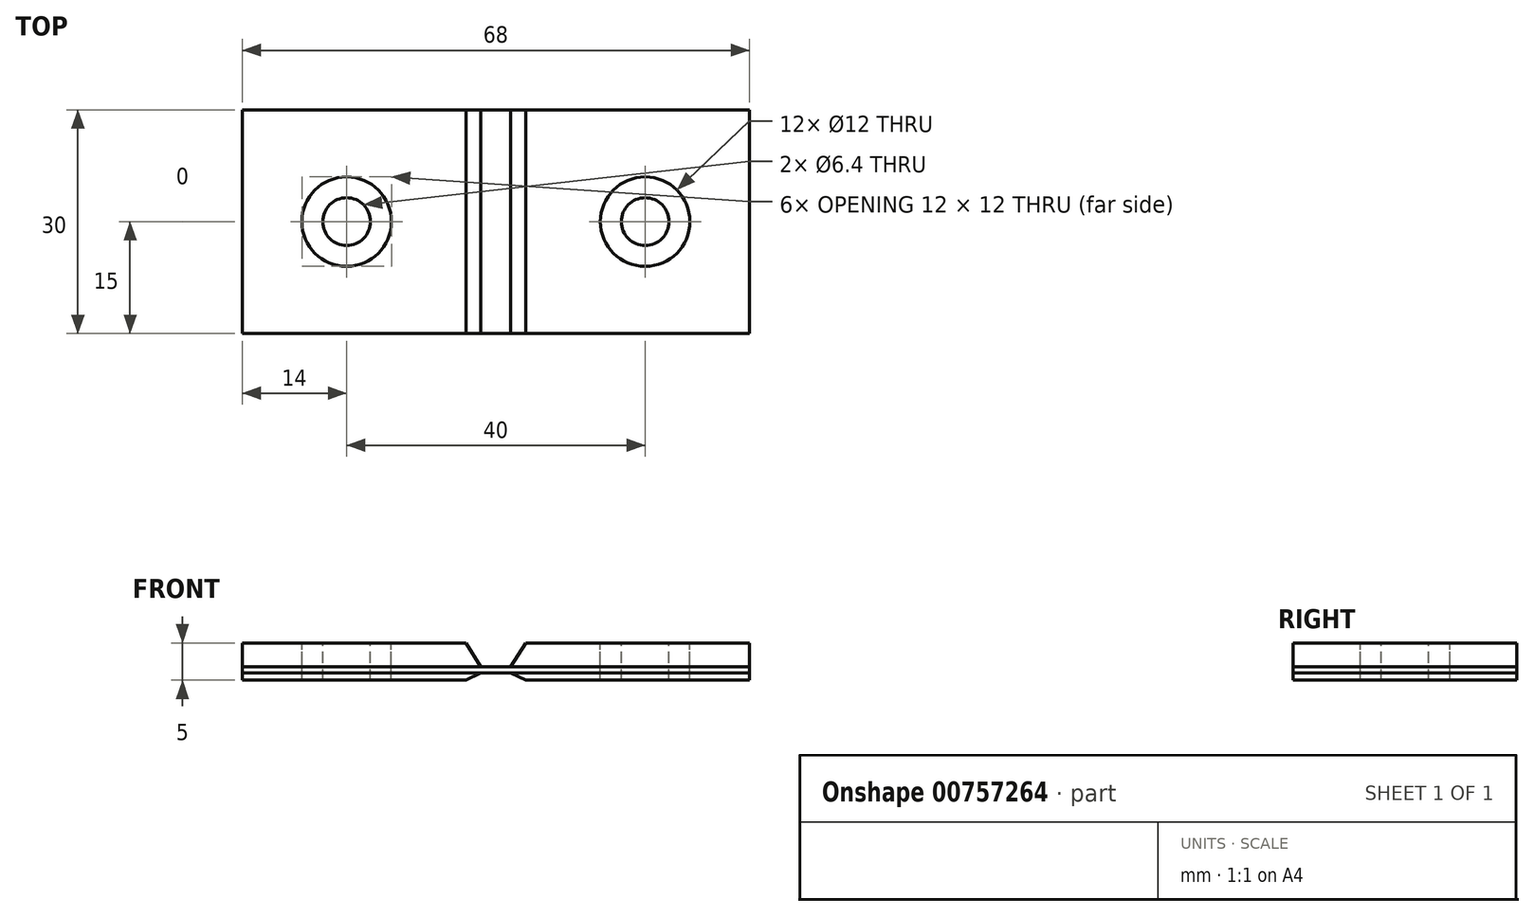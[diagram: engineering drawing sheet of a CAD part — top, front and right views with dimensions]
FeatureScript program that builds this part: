
annotation { "Feature Type Name" : "Feature", "Feature Type Description" : "" }
export const myFeature = defineFeature(function(context is Context, id is Id, definition is map)
    precondition{}
    {
        {
            var Q0;
            Q0=qCreatedBy(makeId("Front.planeOp"),FACE);
            var sketch = newSketch(context, id + "F0", { "sketchPlane" : qUnion([Q0])});
            skLineSegment(sketch, "E0", {"start": v(-34, 0) * mm, "end": v(-34, 5) * mm});
            skLineSegment(sketch, "E1", {"start": v(-34, 5) * mm, "end": v(-4, 5) * mm});
            skLineSegment(sketch, "E2", {"start": v(-4, 5) * mm, "end": v(-2, 1.8) * mm});
            skLineSegment(sketch, "E3", {"start": v(-2, 1.8) * mm, "end": v(2, 1.8) * mm});
            skLineSegment(sketch, "E4", {"start": v(2, 1.8) * mm, "end": v(4, 5) * mm});
            skLineSegment(sketch, "E5", {"start": v(4, 5) * mm, "end": v(34, 5) * mm});
            skLineSegment(sketch, "E6", {"start": v(34, 5) * mm, "end": v(34, 0) * mm});
            skLineSegment(sketch, "E7", {"start": v(34, 0) * mm, "end": v(4, 0) * mm});
            skLineSegment(sketch, "E8", {"start": v(4, 0) * mm, "end": v(2, 1) * mm});
            skLineSegment(sketch, "E9", {"start": v(2, 1) * mm, "end": v(-2, 1) * mm});
            skLineSegment(sketch, "E10", {"start": v(-2, 1) * mm, "end": v(-4, 0) * mm});
            skLineSegment(sketch, "E11", {"start": v(-4, 0) * mm, "end": v(-34, 0) * mm});
            skSolve(sketch);
        }
        {
            var Q0;
            Q0 = qSketchRegion(id + "F0", true);
            extrude(context, id + "F1", {"entities" : qUnion([Q0]), "depth" : 30 * mm, "offsetDistance" : 25 * mm});
        }
        {
            var Q0;
            Q0=makeQuery(id+"F1.opExtrude","CAP_FACE",FACE,{"disambiguationData":[OSD([sQuery(id+"F0.wireOp",EDGE,"E0"),sQuery(id+"F0.wireOp",EDGE,"E1"),sQuery(id+"F0.wireOp",EDGE,"E2"),sQuery(id+"F0.wireOp",EDGE,"E3"),sQuery(id+"F0.wireOp",EDGE,"E4"),sQuery(id+"F0.wireOp",EDGE,"E5"),sQuery(id+"F0.wireOp",EDGE,"E6"),sQuery(id+"F0.wireOp",EDGE,"E7"),sQuery(id+"F0.wireOp",EDGE,"E8"),sQuery(id+"F0.wireOp",EDGE,"E9"),sQuery(id+"F0.wireOp",EDGE,"E10"),sQuery(id+"F0.wireOp",EDGE,"E11")])],"isStart":false});
            var sketch = newSketch(context, id + "F2", { "sketchPlane" : qUnion([Q0])});
            skLineSegment(sketch, "E12.bottom", {"start": v(-34, 1) * mm, "end": v(34, 1) * mm});
            skLineSegment(sketch, "E12.top", {"start": v(-34, 1.8) * mm, "end": v(34, 1.8) * mm});
            skLineSegment(sketch, "E12.left", {"start": v(-34, 1) * mm, "end": v(-34, 1.8) * mm});
            skLineSegment(sketch, "E12.right", {"start": v(34, 1) * mm, "end": v(34, 1.8) * mm});
            skSolve(sketch);
        }
        {
            var Q0;
            Q0 = qSketchRegion(id + "F2", true);
            extrude(context, id + "F3", {"entities" : qUnion([Q0]), "oppositeDirection" : true, "depth" : 30 * mm, "offsetDistance" : 25 * mm});
        }
        {
            var Q0;
            Q0=makeQuery(id+"F3.opExtrude","SWEPT_BODY",BODY,{"disambiguationData":[OSD([sQuery(id+"F2.wireOp",EDGE,"E12.bottom"),sQuery(id+"F2.wireOp",EDGE,"E12.top"),sQuery(id+"F2.wireOp",EDGE,"E12.left"),sQuery(id+"F2.wireOp",EDGE,"E12.right")])]});
            var Q1;
            Q1=makeQuery(id+"F1.opExtrude","SWEPT_BODY",BODY,{"disambiguationData":[OSD([sQuery(id+"F0.wireOp",EDGE,"E0"),sQuery(id+"F0.wireOp",EDGE,"E1"),sQuery(id+"F0.wireOp",EDGE,"E2"),sQuery(id+"F0.wireOp",EDGE,"E3"),sQuery(id+"F0.wireOp",EDGE,"E4"),sQuery(id+"F0.wireOp",EDGE,"E5"),sQuery(id+"F0.wireOp",EDGE,"E6"),sQuery(id+"F0.wireOp",EDGE,"E7"),sQuery(id+"F0.wireOp",EDGE,"E8"),sQuery(id+"F0.wireOp",EDGE,"E9"),sQuery(id+"F0.wireOp",EDGE,"E10"),sQuery(id+"F0.wireOp",EDGE,"E11")])]});
            booleanBodies(context, id + "F4", {"operationType" : BooleanOperationType.SUBTRACTION, "tools" : qUnion([Q0]), "targets" : qUnion([Q1]), "keepTools" : true});
        }
        {
            var Q0;
            Q0=makeQuery(id+"F1.opExtrude","SWEPT_FACE",FACE,{"disambiguationData":[OSD([sQuery(id+"F0.wireOp",EDGE,"E1")])]});
            var sketch = newSketch(context, id + "F5", { "sketchPlane" : qUnion([Q0])});
            skCircle(sketch, "E13", {"center": v(-20, -15) * mm, "radius": 6 * mm});
            skCircle(sketch, "E14", {"center": v(20, -15) * mm, "radius": 6 * mm});
            skSolve(sketch);
        }
        {
            var Q0;
            Q0 = qSketchRegion(id + "F5", true);
            extrude(context, id + "F6", {"entities" : qUnion([Q0]), "operationType" : NewBodyOperationType.REMOVE, "oppositeDirection" : true, "depth" : 25 * mm, "offsetDistance" : 25 * mm});
        }
        {
            var Q0;
            Q0=makeQuery(id+"F1.opExtrude","SWEPT_FACE",FACE,{"disambiguationData":[OSD([sQuery(id+"F0.wireOp",EDGE,"E5")])]});
            var sketch = newSketch(context, id + "F7", { "sketchPlane" : qUnion([Q0])});
            skCircle(sketch, "E15", {"center": v(20, -15) * mm, "radius": 6 * mm});
            skPoint(sketch, "E15.first.point", {"position": v(15.78, -10.73) * mm});
            skPoint(sketch, "E15.second.point", {"position": v(25.84, -13.6) * mm});
            skPoint(sketch, "E15.third.point", {"position": v(19.18, -20.94) * mm});
            skCircle(sketch, "E16", {"center": v(20, -15) * mm, "radius": 3.2 * mm});
            skCircle(sketch, "E17", {"center": v(-20, -15) * mm, "radius": 3.2 * mm});
            skCircle(sketch, "E18", {"center": v(-20, -15) * mm, "radius": 6 * mm});
            skSolve(sketch);
        }
        {
            var Q0;
            Q0 = qSketchRegion(id + "F7", true);
            var Q1;
            Q1=makeQuery(id+"F1.opExtrude","SWEPT_FACE",FACE,{"disambiguationData":[OSD([sQuery(id+"F0.wireOp",EDGE,"E11")])]});
            extrude(context, id + "F8", {"entities" : qUnion([Q0]), "endBound" : BoundingType.UP_TO_SURFACE, "oppositeDirection" : true, "depth" : 25 * mm, "endBoundEntityFace" : qUnion([Q1]), "offsetDistance" : 25 * mm});
        }
    });
